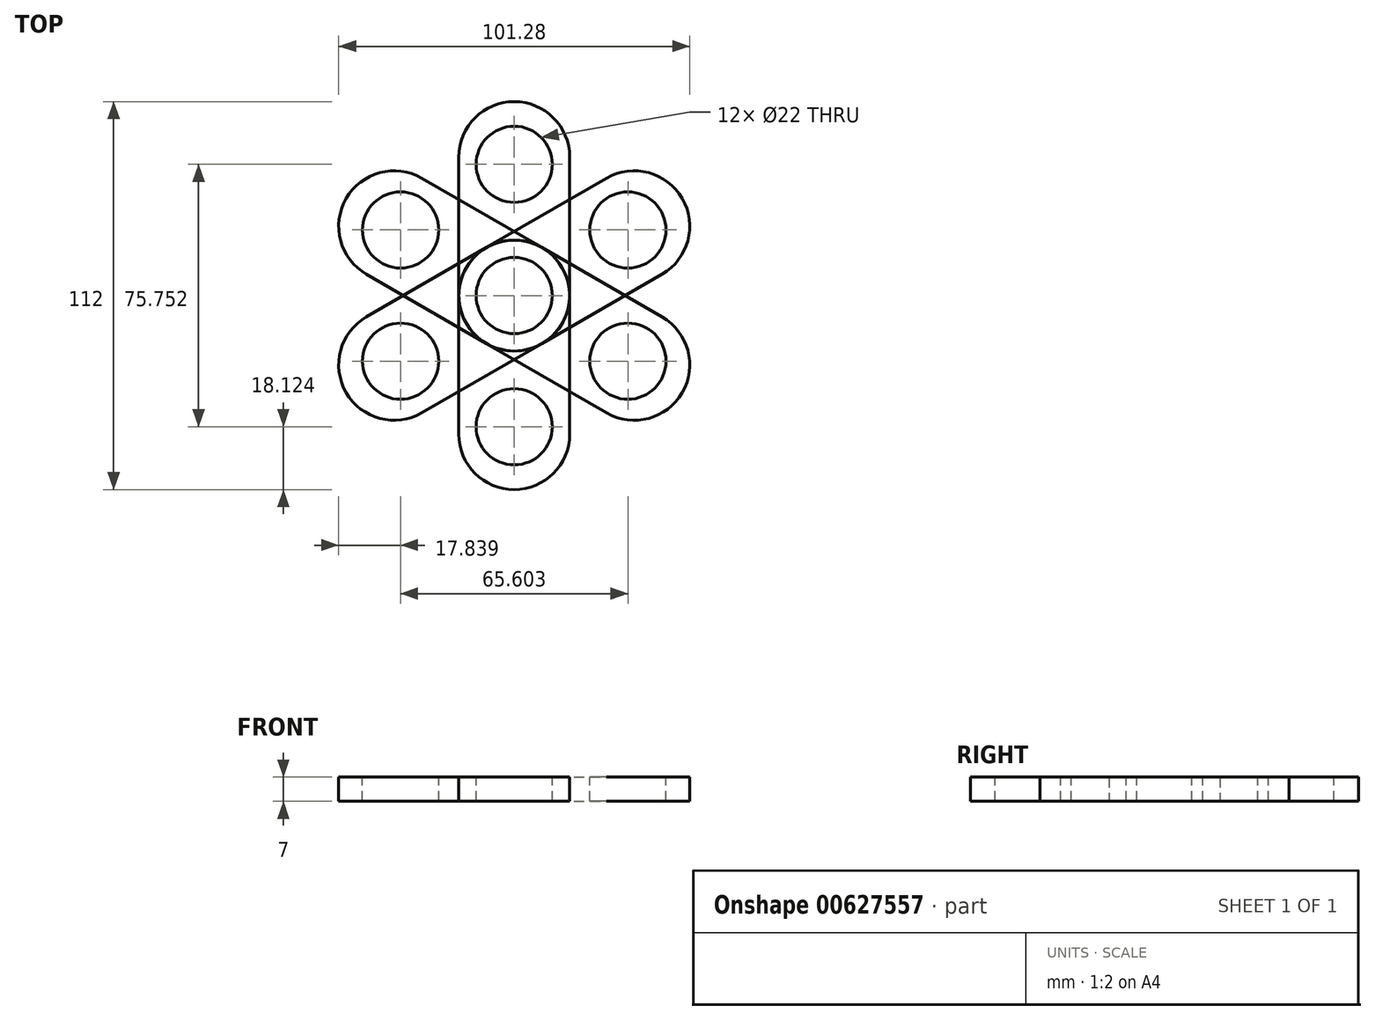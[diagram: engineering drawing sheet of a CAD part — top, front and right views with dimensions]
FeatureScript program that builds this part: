
annotation { "Feature Type Name" : "Feature", "Feature Type Description" : "" }
export const myFeature = defineFeature(function(context is Context, id is Id, definition is map)
    precondition{}
    {
        {
            var Q0;
            Q0=qCreatedBy(makeId("Top.planeOp"),FACE);
            var sketch = newSketch(context, id + "F0", { "sketchPlane" : qUnion([Q0])});
            skCircle(sketch, "E0", {"center": v(0, 0) * mm, "radius": 16 * mm});
            skCircle(sketch, "E1", {"center": v(0, -40) * mm, "radius": 16 * mm});
            skLineSegment(sketch, "E2", {"start": v(16, 0) * mm, "end": v(16, -40) * mm});
            skLineSegment(sketch, "E3", {"start": v(-16, 0) * mm, "end": v(-16, -40) * mm});
            skSolve(sketch);
        }
        {
            var Q0;
            Q0=qSketchRegion(id+"F0",true);
            extrude(context, id + "F1", {"entities" : qUnion([Q0]), "depth" : 7 * mm, "offsetDistance" : 25 * mm});
        }
        {
            var Q0;
            Q0=makeQuery(id+"F1.opExtrude","CAP_FACE",FACE,{"disambiguationData":[OSD([sQuery(id+"F0.wireOp",EDGE,"E0"),sQuery(id+"F0.wireOp",EDGE,"E1"),sQuery(id+"F0.wireOp",EDGE,"E2"),sQuery(id+"F0.wireOp",EDGE,"E3")])],"isStart":false});
            var sketch = newSketch(context, id + "F2", { "sketchPlane" : qUnion([Q0])});
            skCircle(sketch, "E4", {"center": v(0, 0) * mm, "radius": 11 * mm});
            skCircle(sketch, "E5", {"center": v(0, -37.88) * mm, "radius": 11 * mm});
            skSolve(sketch);
        }
        {
            var Q0;
            Q0=qSketchRegion(id+"F2",true);
            extrude(context, id + "F3", {"entities" : qUnion([Q0]), "operationType" : NewBodyOperationType.REMOVE, "endBound" : BoundingType.THROUGH_ALL, "oppositeDirection" : true, "depth" : 25 * mm, "offsetDistance" : 25 * mm});
        }
        {
            var Q0;
            Q0=qCreatedBy(makeId("Front.planeOp"),FACE);
            var sketch = newSketch(context, id + "F4", { "sketchPlane" : qUnion([Q0])});
            skLineSegment(sketch, "E6", {"start": v(0, 0) * mm, "end": v(0, 26.48) * mm});
            skSolve(sketch);
        }
        {
            var Q0;
            Q0=makeQuery(id+"F1.opExtrude","SWEPT_BODY",BODY,{"disambiguationData":[OSD([sQuery(id+"F0.wireOp",EDGE,"E0"),sQuery(id+"F0.wireOp",EDGE,"E1"),sQuery(id+"F0.wireOp",EDGE,"E2"),sQuery(id+"F0.wireOp",EDGE,"E3")])]});
            var Q1;
            Q1=sQuery(id+"F4.wireOp",EDGE,"E6");
            circularPattern(context, id + "F5", {"entities" : qUnion([Q0]), "axis" : qUnion([Q1]), "angle" : 360 * degree, "instanceCount" : 6, "equalSpace" : true});
        }
    });
